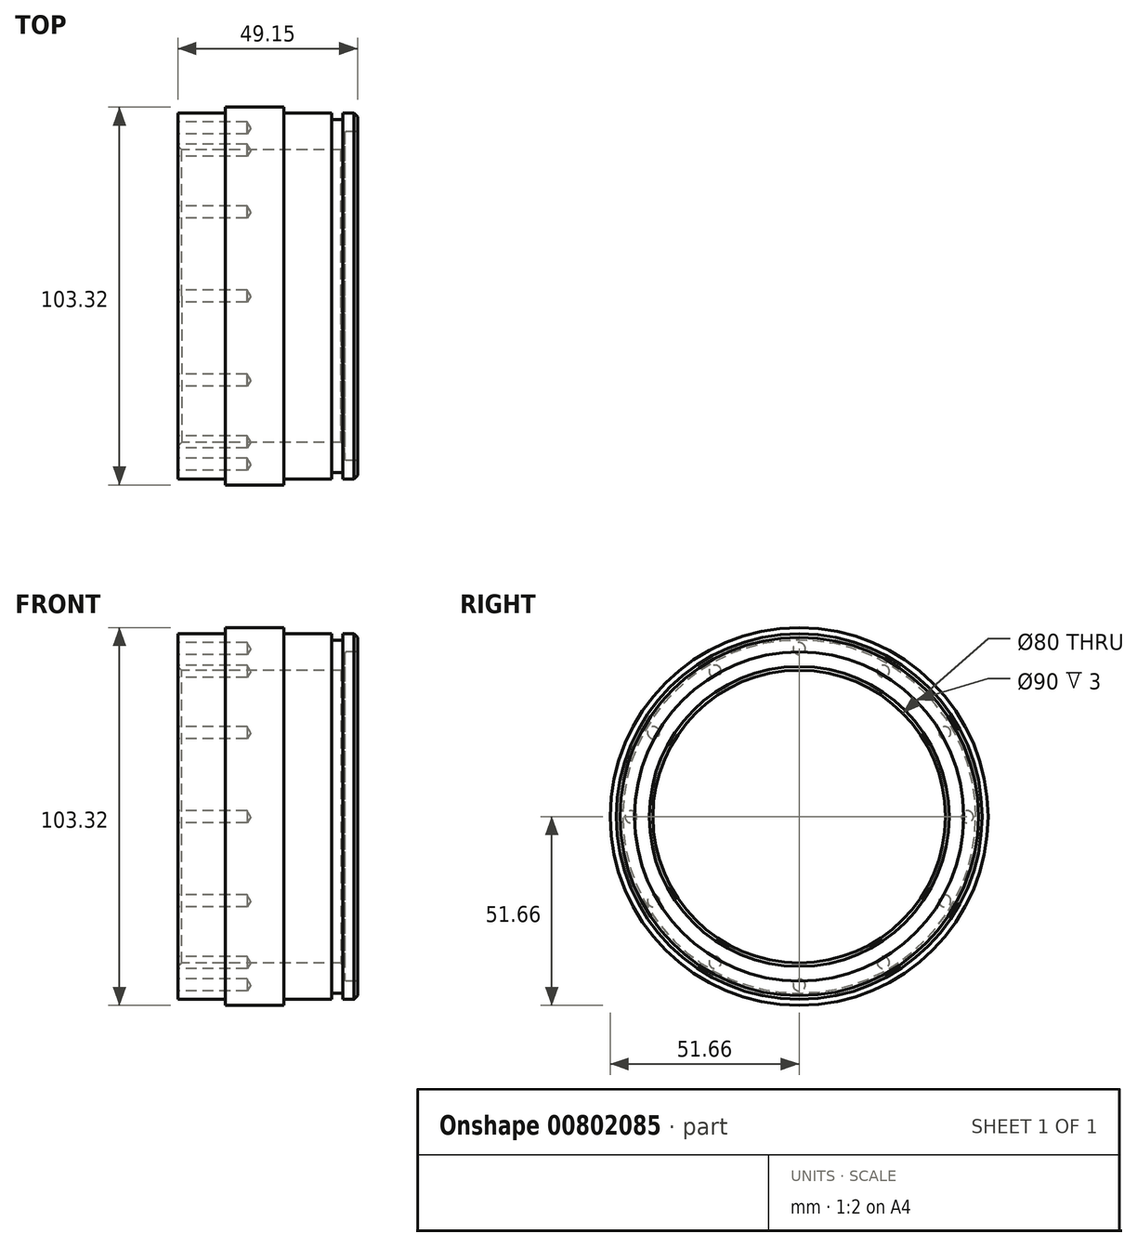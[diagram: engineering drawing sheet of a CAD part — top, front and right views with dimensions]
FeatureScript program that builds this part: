
annotation { "Feature Type Name" : "Feature", "Feature Type Description" : "" }
export const myFeature = defineFeature(function(context is Context, id is Id, definition is map)
    precondition{}
    {
        {
            var Q0;
            Q0=qCreatedBy(makeId("Front.planeOp"),FACE);
            var sketch = newSketch(context, id + "F0", { "sketchPlane" : qUnion([Q0])});
            skLineSegment(sketch, "E0", {"start": v(-26.06, -44.48) * mm, "end": v(52.5, -44.48) * mm, "construction": true});
            skLineSegment(sketch, "E1", {"start": v(-30.1, 5.52) * mm, "end": v(-30.1, -4.48) * mm});
            skLineSegment(sketch, "E2", {"start": v(-30.1, 5.52) * mm, "end": v(-17.6, 5.52) * mm});
            skLineSegment(sketch, "E3", {"start": v(-17.1, 6.02) * mm, "end": v(-17.1, 7.18) * mm});
            skLineSegment(sketch, "E4", {"start": v(-17.1, 7.18) * mm, "end": v(-1.1, 7.18) * mm});
            skLineSegment(sketch, "E5", {"start": v(-1.1, 7.18) * mm, "end": v(-1.1, 6.02) * mm});
            skLineSegment(sketch, "E6", {"start": v(-0.6, 5.52) * mm, "end": v(11.9, 5.52) * mm});
            skLineSegment(sketch, "E7", {"start": v(11.9, 5.52) * mm, "end": v(11.9, 3.77) * mm});
            skLineSegment(sketch, "E8", {"start": v(11.9, 3.77) * mm, "end": v(15.05, 3.77) * mm});
            skLineSegment(sketch, "E9", {"start": v(15.05, 3.77) * mm, "end": v(15.05, 5.52) * mm});
            skLineSegment(sketch, "E10", {"start": v(15.05, 5.52) * mm, "end": v(19.05, 5.52) * mm});
            skLineSegment(sketch, "E11", {"start": v(19.05, 5.52) * mm, "end": v(19.05, 0.52) * mm});
            skLineSegment(sketch, "E12", {"start": v(15.55, -4.48) * mm, "end": v(-30.1, -4.48) * mm});
            skLineSegment(sketch, "E13.top", {"start": v(19.05, 0.52) * mm, "end": v(16.05, 0.52) * mm});
            skLineSegment(sketch, "E13.right", {"start": v(15.55, -4.48) * mm, "end": v(15.55, 0.02) * mm});
            skPoint(sketch, "E14.visualSharp", {"position": v(15.55, 0.52) * mm});
            skArc(sketch, "E14.filletArc", {"start": v(16.05, 0.52) * mm, "mid": v(15.7, 0.37) * mm, "end": v(15.55, 0.02) * mm});
            skPoint(sketch, "E15.visualSharp", {"position": v(-1.1, 5.52) * mm});
            skArc(sketch, "E15.filletArc", {"start": v(-1.1, 6.02) * mm, "mid": v(-0.95, 5.66) * mm, "end": v(-0.6, 5.52) * mm});
            skPoint(sketch, "E16.visualSharp", {"position": v(-17.1, 5.52) * mm});
            skArc(sketch, "E16.filletArc", {"start": v(-17.6, 5.52) * mm, "mid": v(-17.24, 5.66) * mm, "end": v(-17.1, 6.02) * mm});
            skSolve(sketch);
        }
        {
            var Q0;
            Q0 = qSketchRegion(id + "F0", true);
            var Q1;
            Q1=sQuery(id+"F0.wireOp",EDGE,"E0");
            revolve(context, id + "F1", {"entities" : qUnion([Q0]), "axis" : qUnion([Q1]), "revolveType" : RevolveType.FULL});
        }
        {
            var Q0;
            Q0=makeQuery(id+"F1.opRevolve","SWEPT_BODY",BODY,{"disambiguationData":[OSD([sQuery(id+"F0.wireOp",EDGE,"E1"),sQuery(id+"F0.wireOp",EDGE,"E2"),sQuery(id+"F0.wireOp",EDGE,"E3"),sQuery(id+"F0.wireOp",EDGE,"E4"),sQuery(id+"F0.wireOp",EDGE,"E5"),sQuery(id+"F0.wireOp",EDGE,"E6"),sQuery(id+"F0.wireOp",EDGE,"E7"),sQuery(id+"F0.wireOp",EDGE,"E8"),sQuery(id+"F0.wireOp",EDGE,"E9"),sQuery(id+"F0.wireOp",EDGE,"E10"),sQuery(id+"F0.wireOp",EDGE,"E11"),sQuery(id+"F0.wireOp",EDGE,"E12")])]});
            transform(context, id + "F2", {"entities" : qUnion([Q0]), "transformType" : TransformType.TRANSLATION_3D, "dx" : 0 * mm, "dy" : 0 * mm, "dz" : 44.56 * mm, "makeCopy" : false});
        }
        {
            var Q0;
            Q0=makeQuery(id+"F1.opRevolve","SWEPT_FACE",FACE,{"disambiguationData":[OSD([sQuery(id+"F0.wireOp",EDGE,"E1")])]});
            var sketch = newSketch(context, id + "F3", { "sketchPlane" : qUnion([Q0])});
            skLineSegment(sketch, "E17", {"start": v(0, 0) * mm, "end": v(0, 46) * mm, "construction": true});
            skPoint(sketch, "E18", {"position": v(0, 46) * mm});
            skPoint(sketch, "E19.1.0", {"position": v(-23, 39.84) * mm});
            skPoint(sketch, "E19.2.0", {"position": v(-39.84, 23) * mm});
            skPoint(sketch, "E19.3.0", {"position": v(-46, 0) * mm});
            skPoint(sketch, "E19.4.0", {"position": v(-39.84, -23) * mm});
            skPoint(sketch, "E19.5.0", {"position": v(-23, -39.84) * mm});
            skPoint(sketch, "E19.6.0", {"position": v(0, -46) * mm});
            skPoint(sketch, "E19.7.0", {"position": v(23, -39.84) * mm});
            skPoint(sketch, "E19.8.0", {"position": v(39.84, -23) * mm});
            skPoint(sketch, "E19.9.0", {"position": v(46, 0) * mm});
            skPoint(sketch, "E19.10.0", {"position": v(39.84, 23) * mm});
            skPoint(sketch, "E19.11.0", {"position": v(23, 39.84) * mm});
            skPoint(sketch, "E19.center", {"position": v(0, 0) * mm});
            skSolve(sketch);
        }
        {
            var Q0;
            Q0=sQuery(id+"F3.wireOp",VERTEX,"E18");
            var Q1;
            Q1=sQuery(id+"F3.wireOp",VERTEX,"E19.11.0");
            var Q2;
            Q2=sQuery(id+"F3.wireOp",VERTEX,"E19.10.0");
            var Q3;
            Q3=sQuery(id+"F3.wireOp",VERTEX,"E19.9.0");
            var Q4;
            Q4=sQuery(id+"F3.wireOp",VERTEX,"E19.8.0");
            var Q5;
            Q5=sQuery(id+"F3.wireOp",VERTEX,"E19.7.0");
            var Q6;
            Q6=sQuery(id+"F3.wireOp",VERTEX,"E19.6.0");
            var Q7;
            Q7=sQuery(id+"F3.wireOp",VERTEX,"E19.5.0");
            var Q8;
            Q8=sQuery(id+"F3.wireOp",VERTEX,"E19.4.0");
            var Q9;
            Q9=sQuery(id+"F3.wireOp",VERTEX,"E19.3.0");
            var Q10;
            Q10=sQuery(id+"F3.wireOp",VERTEX,"E19.2.0");
            var Q11;
            Q11=sQuery(id+"F3.wireOp",VERTEX,"E19.1.0");
            var Q12;
            Q12=makeQuery(id+"F1.opRevolve","SWEPT_BODY",BODY,{"disambiguationData":[OSD([sQuery(id+"F0.wireOp",EDGE,"E1"),sQuery(id+"F0.wireOp",EDGE,"E2"),sQuery(id+"F0.wireOp",EDGE,"E3"),sQuery(id+"F0.wireOp",EDGE,"E4"),sQuery(id+"F0.wireOp",EDGE,"E5"),sQuery(id+"F0.wireOp",EDGE,"E6"),sQuery(id+"F0.wireOp",EDGE,"E7"),sQuery(id+"F0.wireOp",EDGE,"E8"),sQuery(id+"F0.wireOp",EDGE,"E9"),sQuery(id+"F0.wireOp",EDGE,"E10"),sQuery(id+"F0.wireOp",EDGE,"E11"),sQuery(id+"F0.wireOp",EDGE,"E12")])]});
            hole(context, id + "F4", {"style" : HoleStyle.SIMPLE, "endStyle" : HoleEndStyle.BLIND, "standardTappedOrClearance" : lookupTablePath({ "standard" : "ISO", "engagement" : "75%", "pitch" : "0.7 mm", "size" : "M4", "type" : "Tapped" }), "standardBlindInLast" : lookupTablePath({ "standard" : "ISO", "engagement" : "75%", "pitch" : "0.7 mm", "size" : "M4", "type" : "Tapped" }), "holeDiameter" : 3.3 * mm, "showTappedDepth" : true, "holeDepth" : 18.93 * mm, "tappedDepth" : 16.82 * mm, "tapClearance" : 3, "startFromSketch" : true, "locations" : qUnion([Q0, Q1, Q2, Q3, Q4, Q5, Q6, Q7, Q8, Q9, Q10, Q11]), "scope" : qUnion([Q12]), "majorDiameter" : 4 * mm});
        }
        {
            var Q0;
            Q0=makeQuery(id+"F1.opRevolve","SWEPT_FACE",FACE,{"disambiguationData":[OSD([sQuery(id+"F0.wireOp",EDGE,"E12")])]});
            var Q1;
            Q1=makeQuery(id+"F1.opRevolve","SWEPT_EDGE",EDGE,{"disambiguationData":[OSD([sQuery(id+"F0.wireOp",EDGE,"E10"),sQuery(id+"F0.wireOp",EDGE,"E11")])]});
            chamfer(context, id + "F5", {"entities" : qUnion([Q0, Q1]), "width" : 1 * mm, "tangentPropagation" : true});
        }
    });
